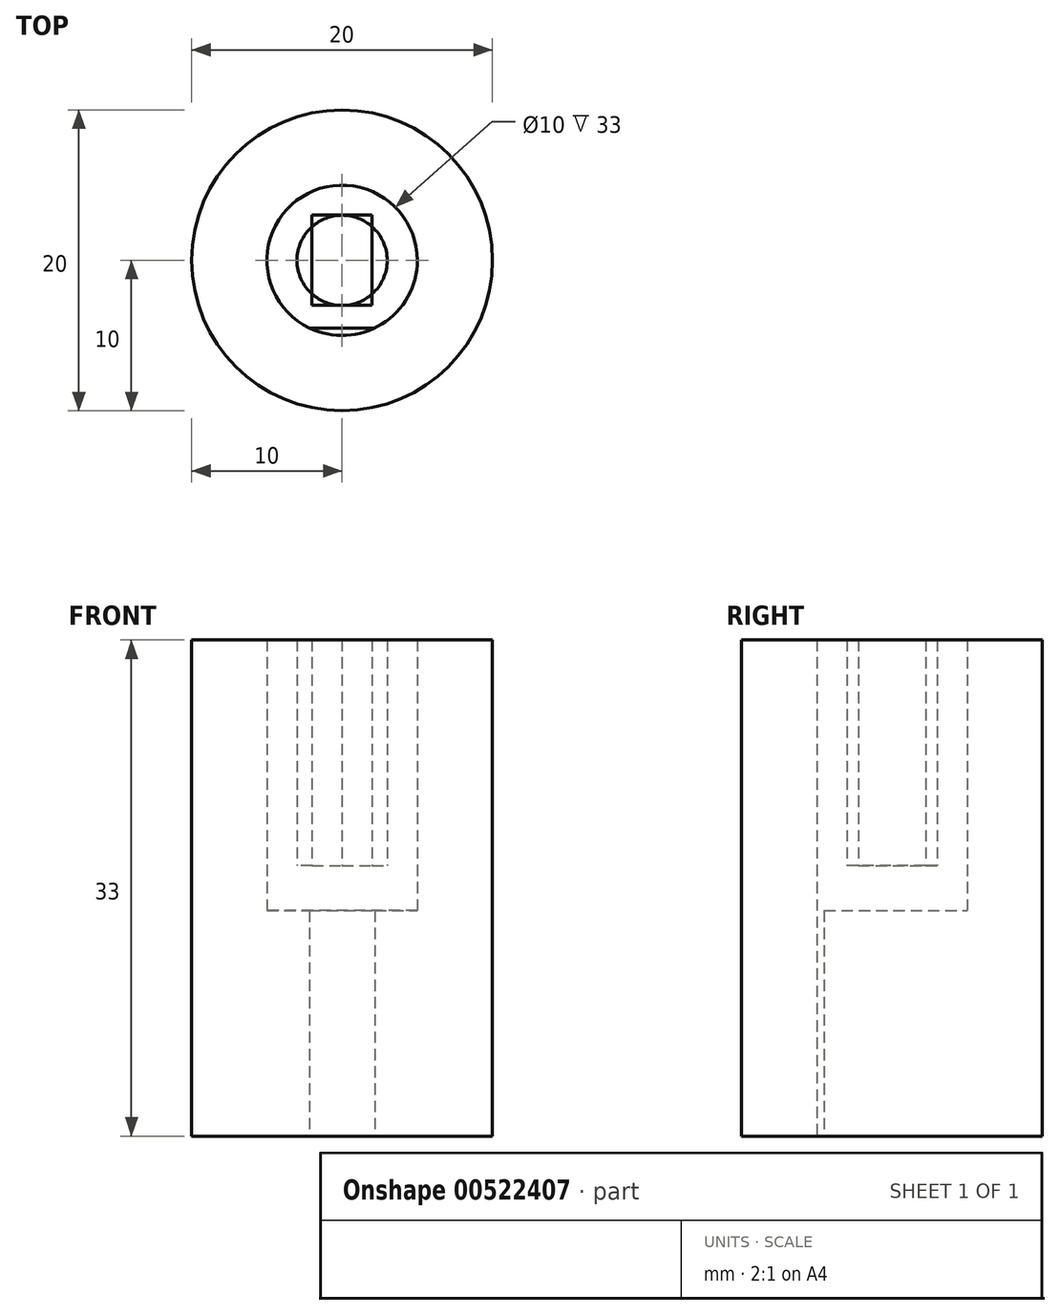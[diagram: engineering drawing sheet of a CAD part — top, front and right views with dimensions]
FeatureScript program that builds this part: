
annotation { "Feature Type Name" : "Feature", "Feature Type Description" : "" }
export const myFeature = defineFeature(function(context is Context, id is Id, definition is map)
    precondition{}
    {
        {
            var Q0;
            Q0=qCreatedBy(makeId("Top.planeOp"),FACE);
            var sketch = newSketch(context, id + "F0", { "sketchPlane" : qUnion([Q0])});
            skCircle(sketch, "E0", {"center": v(0, 0) * mm, "radius": 10 * mm});
            skSolve(sketch);
        }
        {
            var Q0;
            Q0=makeQuery(id+"F0.imprint","IMPRINT",FACE,{"disambiguationData":[TD([[makeQuery(id+"F0.imprint","IMPRINT",EDGE,{"derivedFrom":sQuery(id+"F0.wireOp",EDGE,"E0")}),1.0]])]});
            extrude(context, id + "F1", {"entities" : qUnion([Q0]), "depth" : 18 * mm, "offsetDistance" : 25 * mm});
        }
        {
            var Q0;
            Q0=makeQuery(id+"F1.opExtrude","CAP_FACE",FACE,{"disambiguationData":[OSD([sQuery(id+"F0.wireOp",EDGE,"E0")])],"isStart":true});
            var sketch = newSketch(context, id + "F2", { "sketchPlane" : qUnion([Q0])});
            skCircle(sketch, "E1", {"center": v(0, 0) * mm, "radius": 5 * mm});
            skLineSegment(sketch, "E2.bottom", {"start": v(-3.5, 4.5) * mm, "end": v(3.5, 4.5) * mm});
            skLineSegment(sketch, "E2.top", {"start": v(-3.5, -4.5) * mm, "end": v(3.5, -4.5) * mm});
            skLineSegment(sketch, "E2.left", {"start": v(-3.5, 4.5) * mm, "end": v(-3.5, -4.5) * mm});
            skLineSegment(sketch, "E2.right", {"start": v(3.5, 4.5) * mm, "end": v(3.5, -4.5) * mm});
            skSolve(sketch);
        }
        {
            var Q0;
            {var subQ1=sQuery(id+"F2.wireOp",EDGE,"E1");var subQ9=sQuery(id+"F2.wireOp",EDGE,"E2.bottom");var subQ11=makeQuery(id+"F2.imprint","INTERSECT",VERTEX,{"disambiguationData":[OD(0.0)],"derivedFrom":[subQ1,subQ9]});Q0=makeQuery(id+"F2.imprint","IMPRINT",FACE,{"disambiguationData":[TD([[makeQuery(id+"F2.imprint","IMPRINT",EDGE,{"disambiguationData":[TD([[subQ11,1.0]])],"derivedFrom":subQ1}),1.0]])]});}
            extrude(context, id + "F3", {"entities" : qUnion([Q0]), "operationType" : NewBodyOperationType.REMOVE, "oppositeDirection" : true, "depth" : 15 * mm, "offsetDistance" : 25 * mm});
        }
        {
            var Q0;
            Q0=makeQuery(id+"F1.opExtrude","CAP_FACE",FACE,{"disambiguationData":[OSD([sQuery(id+"F0.wireOp",EDGE,"E0")])],"isStart":false});
            var sketch = newSketch(context, id + "F4", { "sketchPlane" : qUnion([Q0])});
            skCircle(sketch, "E3", {"center": v(0, 0) * mm, "radius": 5 * mm});
            skSolve(sketch);
        }
        {
            var Q0;
            Q0=makeQuery(id+"F4.imprint","IMPRINT",FACE,{"disambiguationData":[TD([[makeQuery(id+"F4.imprint","IMPRINT",EDGE,{"derivedFrom":sQuery(id+"F4.wireOp",EDGE,"E3")}),1.0]])]});
            extrude(context, id + "F5", {"entities" : qUnion([Q0]), "operationType" : NewBodyOperationType.REMOVE, "oppositeDirection" : true, "depth" : 3 * mm, "offsetDistance" : 25 * mm});
        }
        {
            var Q0;
            Q0=makeQuery(id+"F1.opExtrude","CAP_FACE",FACE,{"disambiguationData":[OSD([sQuery(id+"F0.wireOp",EDGE,"E0")])],"isStart":false});
            var sketch = newSketch(context, id + "F6", { "sketchPlane" : qUnion([Q0])});
            skCircle(sketch, "E4", {"center": v(0, 0) * mm, "radius": 3 * mm});
            skLineSegment(sketch, "E5.bottom", {"start": v(-2, 3) * mm, "end": v(2, 3) * mm});
            skLineSegment(sketch, "E5.top", {"start": v(-2, -3) * mm, "end": v(2, -3) * mm});
            skLineSegment(sketch, "E5.left", {"start": v(-2, 3) * mm, "end": v(-2, -3) * mm});
            skLineSegment(sketch, "E5.right", {"start": v(2, 3) * mm, "end": v(2, -3) * mm});
            skSolve(sketch);
        }
        {
            var Q0;
            Q0=makeQuery(id+"F6.imprint","IMPRINT",FACE,{"disambiguationData":[TD([[makeQuery(id+"F6.imprint","IMPRINT",EDGE,{"derivedFrom":makeQuery(id+"F1.opExtrude","CAP_EDGE",EDGE,{"disambiguationData":[OSD([sQuery(id+"F0.wireOp",EDGE,"E0")])],"isStart":false})}),1.0]])]});
            var Q1;
            Q1=makeQuery(id+"F6.imprint","IMPRINT",FACE,{"disambiguationData":[TD([[makeQuery(id+"F6.imprint","IMPRINT",EDGE,{"derivedFrom":makeQuery(id+"F5.boolean.opBoolean","COPY",EDGE,{"derivedFrom":makeQuery(id+"F5.opExtrude","CAP_EDGE",EDGE,{"disambiguationData":[OSD([sQuery(id+"F4.wireOp",EDGE,"E3")])],"isStart":true})})}),1.0]])]});
            var Q2;
            {var subQ0=sQuery(id+"F6.wireOp",EDGE,"E5.right");var subQ1=sQuery(id+"F6.wireOp",EDGE,"E4");var subQ2=makeQuery(id+"F6.imprint","INTERSECT",VERTEX,{"disambiguationData":[OD(0.0)],"derivedFrom":[subQ1,subQ0]});Q2=makeQuery(id+"F6.imprint","IMPRINT",FACE,{"disambiguationData":[TD([[makeQuery(id+"F6.imprint","IMPRINT",EDGE,{"disambiguationData":[TD([[subQ2,1.0]])],"derivedFrom":subQ1}),1.0]])]});}
            var Q3;
            {var subQ0=sQuery(id+"F6.wireOp",EDGE,"E5.top");var subQ1=sQuery(id+"F6.wireOp",EDGE,"E4");var subQ2=makeQuery(id+"F6.imprint","INTERSECT",VERTEX,{"derivedFrom":[subQ1,subQ0]});Q3=makeQuery(id+"F6.imprint","IMPRINT",FACE,{"disambiguationData":[TD([[makeQuery(id+"F6.imprint","IMPRINT",EDGE,{"disambiguationData":[TD([[subQ2,-1.0]])],"derivedFrom":subQ1}),-1.0]])]});}
            var Q4;
            {var subQ0=sQuery(id+"F6.wireOp",EDGE,"E5.left");var subQ1=sQuery(id+"F6.wireOp",EDGE,"E4");var subQ2=makeQuery(id+"F6.imprint","INTERSECT",VERTEX,{"disambiguationData":[OD(1.0)],"derivedFrom":[subQ1,subQ0]});Q4=makeQuery(id+"F6.imprint","IMPRINT",FACE,{"disambiguationData":[TD([[makeQuery(id+"F6.imprint","IMPRINT",EDGE,{"disambiguationData":[TD([[subQ2,-1.0]])],"derivedFrom":subQ1}),-1.0]])]});}
            var Q5;
            {var subQ0=sQuery(id+"F6.wireOp",EDGE,"E5.left");var subQ1=sQuery(id+"F6.wireOp",EDGE,"E4");var subQ2=makeQuery(id+"F6.imprint","INTERSECT",VERTEX,{"disambiguationData":[OD(0.0)],"derivedFrom":[subQ1,subQ0]});Q5=makeQuery(id+"F6.imprint","IMPRINT",FACE,{"disambiguationData":[TD([[makeQuery(id+"F6.imprint","IMPRINT",EDGE,{"disambiguationData":[TD([[subQ2,-1.0]])],"derivedFrom":subQ1}),1.0]])]});}
            var Q6;
            {var subQ0=sQuery(id+"F6.wireOp",EDGE,"E5.bottom");var subQ1=sQuery(id+"F6.wireOp",EDGE,"E4");var subQ2=makeQuery(id+"F6.imprint","INTERSECT",VERTEX,{"derivedFrom":[subQ1,subQ0]});Q6=makeQuery(id+"F6.imprint","IMPRINT",FACE,{"disambiguationData":[TD([[makeQuery(id+"F6.imprint","IMPRINT",EDGE,{"disambiguationData":[TD([[subQ2,-1.0]])],"derivedFrom":subQ1}),-1.0]])]});}
            var Q7;
            {var subQ0=sQuery(id+"F6.wireOp",EDGE,"E5.bottom");var subQ1=sQuery(id+"F6.wireOp",EDGE,"E4");var subQ2=makeQuery(id+"F6.imprint","INTERSECT",VERTEX,{"derivedFrom":[subQ1,subQ0]});Q7=makeQuery(id+"F6.imprint","IMPRINT",FACE,{"disambiguationData":[TD([[makeQuery(id+"F6.imprint","IMPRINT",EDGE,{"disambiguationData":[TD([[subQ2,1.0]])],"derivedFrom":subQ1}),-1.0]])]});}
            extrude(context, id + "F7", {"entities" : qUnion([Q0, Q1, Q2, Q3, Q4, Q5, Q6, Q7]), "operationType" : NewBodyOperationType.ADD, "depth" : 15 * mm, "offsetDistance" : 25 * mm});
        }
    });
